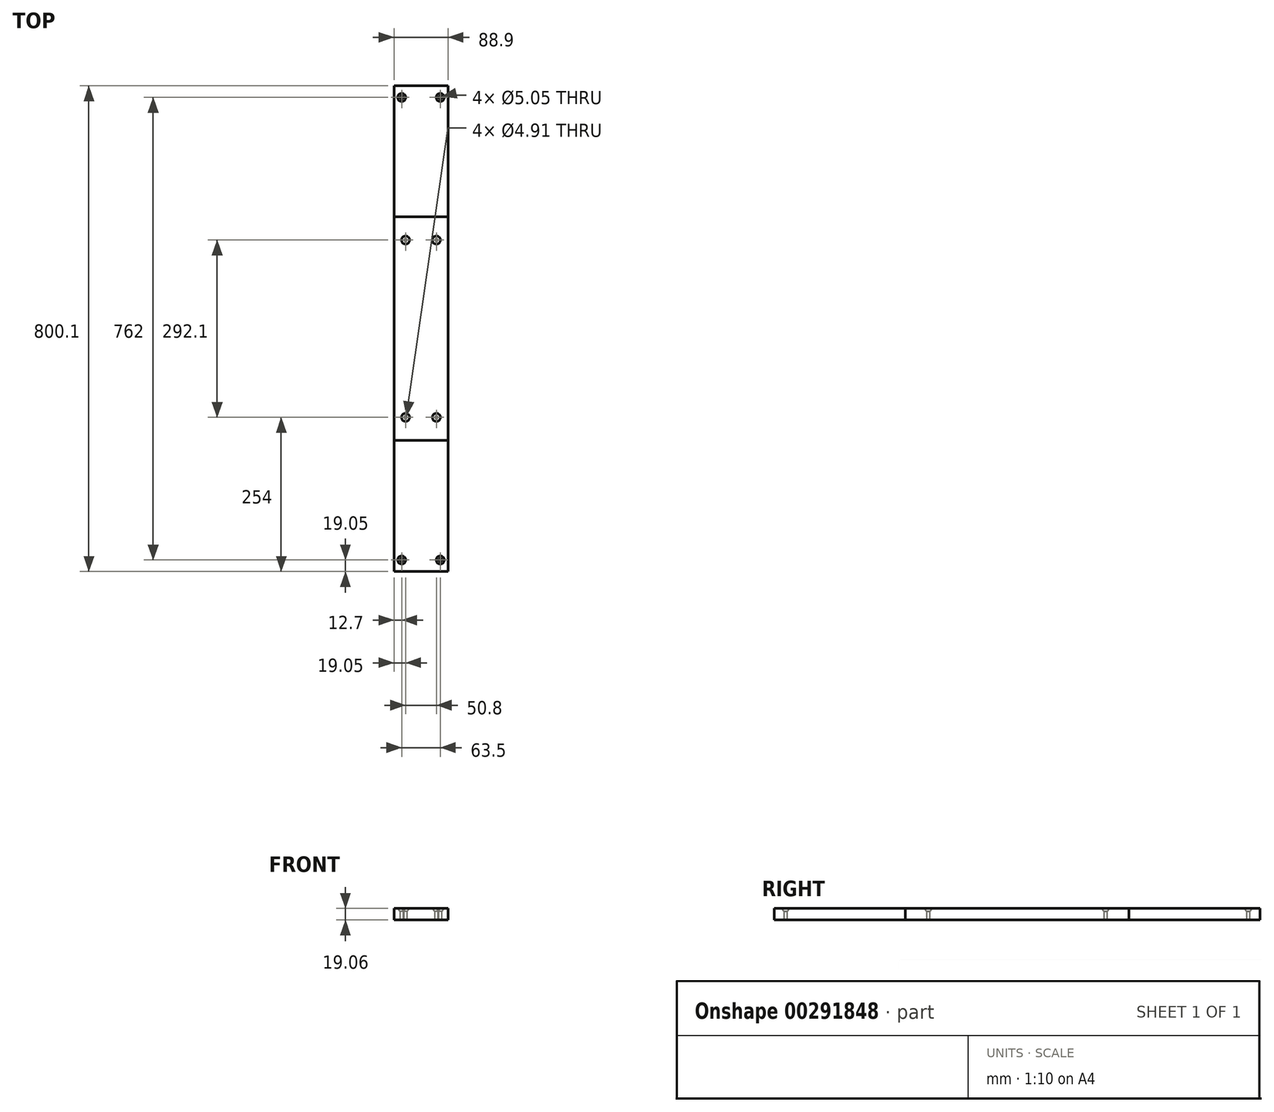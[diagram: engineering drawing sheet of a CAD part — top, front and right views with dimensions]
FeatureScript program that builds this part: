
annotation { "Feature Type Name" : "Feature", "Feature Type Description" : "" }
export const myFeature = defineFeature(function(context is Context, id is Id, definition is map)
    precondition{}
    {
        {
            var Q0;
            Q0=qCreatedBy(makeId("Front.planeOp"),FACE);
            var sketch = newSketch(context, id + "F0", { "sketchPlane" : qUnion([Q0])});
            skLineSegment(sketch, "E0.bottom", {"start": v(44.45, -9.52) * mm, "end": v(-44.45, -9.53) * mm});
            skLineSegment(sketch, "E0.top", {"start": v(44.45, 9.53) * mm, "end": v(-44.45, 9.53) * mm});
            skLineSegment(sketch, "E0.left", {"start": v(44.45, -9.52) * mm, "end": v(44.45, 9.53) * mm});
            skLineSegment(sketch, "E0.right", {"start": v(-44.45, -9.53) * mm, "end": v(-44.45, 9.52) * mm});
            skPoint(sketch, "E0.middle", {"position": v(0, 0) * mm});
            skSolve(sketch);
        }
        {
            var Q0;
            Q0 = qSketchRegion(id + "F0", true);
            extrude(context, id + "F1", {"entities" : qUnion([Q0]), "endBound" : BoundingType.SYMMETRIC, "depth" : 368.3 * mm});
        }
        {
            var Q0;
            Q0=makeQuery(id+"F1.opExtrude","SWEPT_FACE",FACE,{"disambiguationData":[OSD([sQuery(id+"F0.wireOp",EDGE,"E0.top")])]});
            var sketch = newSketch(context, id + "F2", { "sketchPlane" : qUnion([Q0])});
            skLineSegment(sketch, "E1", {"start": v(-25.4, -146.05) * mm, "end": v(25.4, -146.05) * mm});
            skLineSegment(sketch, "E2.MirrorCS", {"start": v(-25.4, 146.05) * mm, "end": v(25.4, 146.05) * mm});
            skSolve(sketch);
        }
        {
            var Q0;
            Q0=sQuery(id+"F2.wireOp",VERTEX,"E1.start");
            var Q1;
            Q1=sQuery(id+"F2.wireOp",VERTEX,"E1.end");
            var Q2;
            Q2=sQuery(id+"F2.wireOp",VERTEX,"E2.MirrorCS.start");
            var Q3;
            Q3=sQuery(id+"F2.wireOp",VERTEX,"E2.MirrorCS.end");
            var Q4;
            Q4=makeQuery(id+"F1.opExtrude","SWEPT_BODY",BODY,{"disambiguationData":[OSD([sQuery(id+"F0.wireOp",EDGE,"E0.bottom"),sQuery(id+"F0.wireOp",EDGE,"E0.top"),sQuery(id+"F0.wireOp",EDGE,"E0.left"),sQuery(id+"F0.wireOp",EDGE,"E0.right")])]});
            hole(context, id + "F3", {"style" : HoleStyle.C_SINK, "endStyle" : HoleEndStyle.THROUGH, "standardTappedOrClearance" : lookupTablePath({ "standard" : "ANSI", "size" : "#10 (0.2)", "type" : "Drilled" }), "standardBlindInLast" : lookupTablePath({ "standard" : "ANSI", "size" : "#10", "type" : "Drilled" }), "holeDiameter" : 4.9 * mm, "cSinkDiameter" : 13.5 * mm, "cSinkAngle" : 82 * degree, "tappedDepth" : 12.7 * mm, "tapClearance" : 3, "locations" : qUnion([Q0, Q1, Q2, Q3]), "scope" : qUnion([Q4])});
        }
        {
            var Q0;
            Q0 = qSketchRegion(id + "F0", true);
            extrude(context, id + "F4", {"entities" : qUnion([Q0]), "endBound" : BoundingType.SYMMETRIC, "depth" : 800.1 * mm});
        }
        {
            var Q0;
            Q0=makeQuery(id+"F4.opExtrude","SWEPT_FACE",FACE,{"disambiguationData":[OSD([sQuery(id+"F0.wireOp",EDGE,"E0.top")])]});
            var sketch = newSketch(context, id + "F5", { "sketchPlane" : qUnion([Q0])});
            skLineSegment(sketch, "E3", {"start": v(-31.75, -381) * mm, "end": v(31.75, -381) * mm});
            skLineSegment(sketch, "E4.MirrorCS", {"start": v(-31.75, 381) * mm, "end": v(31.75, 381) * mm});
            skSolve(sketch);
        }
        {
            var Q0;
            Q0=sQuery(id+"F5.wireOp",VERTEX,"E3.start");
            var Q1;
            Q1=sQuery(id+"F5.wireOp",VERTEX,"E3.end");
            var Q2;
            Q2=sQuery(id+"F5.wireOp",VERTEX,"E4.MirrorCS.start");
            var Q3;
            Q3=sQuery(id+"F5.wireOp",VERTEX,"E4.MirrorCS.end");
            var Q4;
            Q4=makeQuery(id+"F4.opExtrude","SWEPT_BODY",BODY,{"disambiguationData":[OSD([sQuery(id+"F0.wireOp",EDGE,"E0.bottom"),sQuery(id+"F0.wireOp",EDGE,"E0.top"),sQuery(id+"F0.wireOp",EDGE,"E0.left"),sQuery(id+"F0.wireOp",EDGE,"E0.right")])]});
            hole(context, id + "F6", {"style" : HoleStyle.C_SINK, "endStyle" : HoleEndStyle.THROUGH, "standardTappedOrClearance" : lookupTablePath({ "standard" : "ANSI", "size" : "#8 (0.2)", "type" : "Drilled" }), "standardBlindInLast" : lookupTablePath({ "standard" : "ANSI", "size" : "#8", "type" : "Drilled" }), "holeDiameter" : 5.05 * mm, "cSinkDiameter" : 13.5 * mm, "cSinkAngle" : 82 * degree, "tappedDepth" : 12.7 * mm, "tapClearance" : 3, "locations" : qUnion([Q0, Q1, Q2, Q3]), "scope" : qUnion([Q4])});
        }
    });
